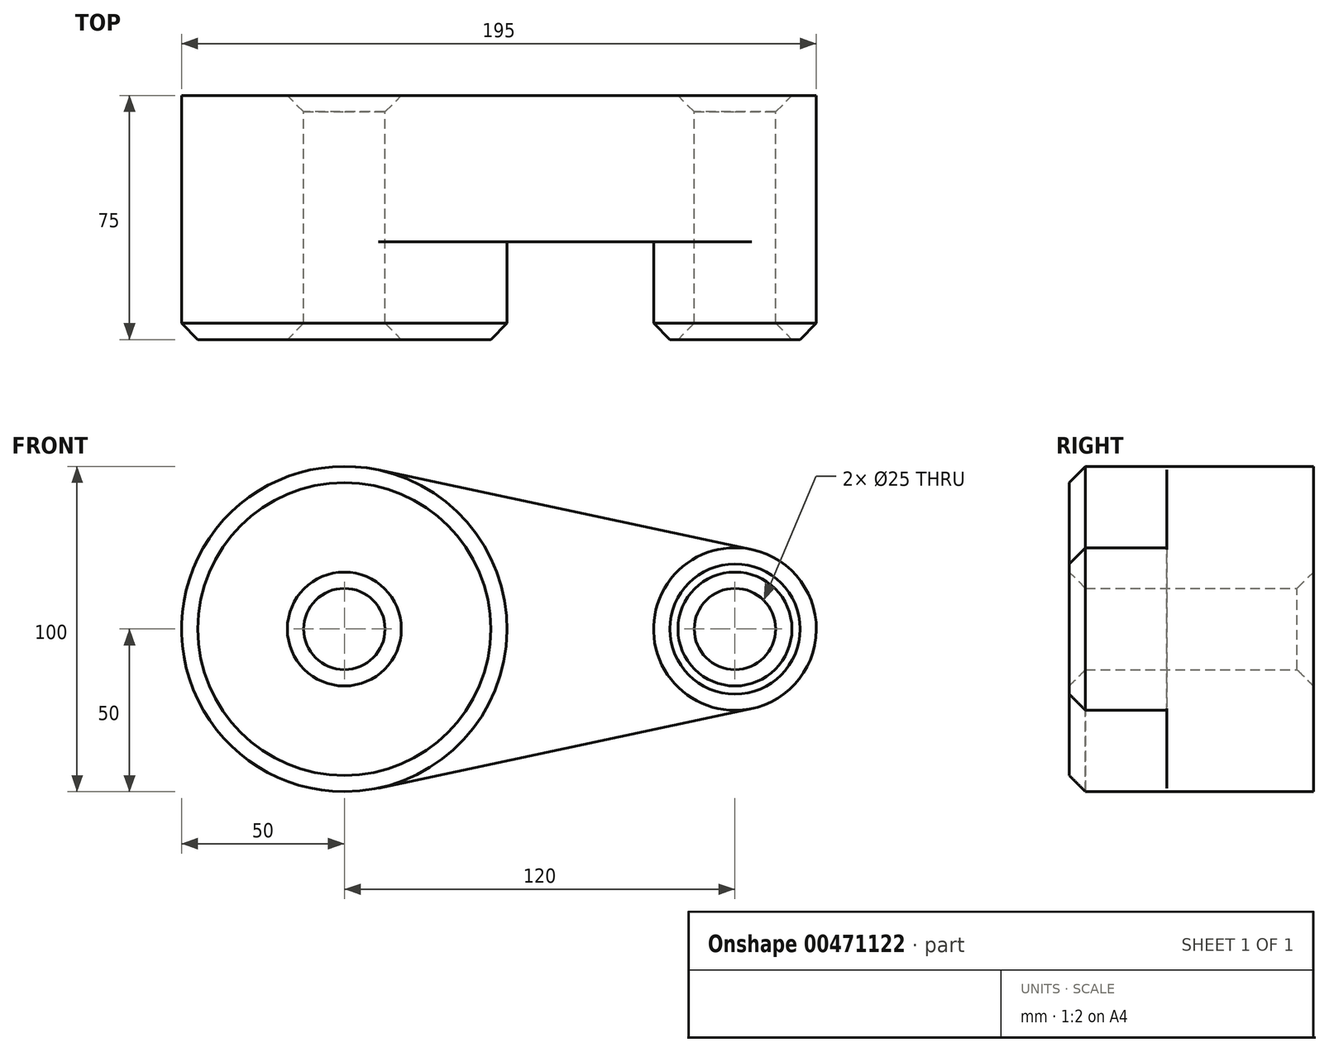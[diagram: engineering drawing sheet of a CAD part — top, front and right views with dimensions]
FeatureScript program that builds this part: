
annotation { "Feature Type Name" : "Feature", "Feature Type Description" : "" }
export const myFeature = defineFeature(function(context is Context, id is Id, definition is map)
    precondition{}
    {
        {
            var Q0;
            Q0=qCreatedBy(makeId("Front.planeOp"),FACE);
            var sketch = newSketch(context, id + "F0", { "sketchPlane" : qUnion([Q0])});
            skCircle(sketch, "E0", {"center": v(0, 0) * mm, "radius": 50 * mm});
            skCircle(sketch, "E1", {"center": v(120, 0) * mm, "radius": 25 * mm});
            skLineSegment(sketch, "E2", {"start": v(10.42, 48.9) * mm, "end": v(125.2, 24.45) * mm});
            skLineSegment(sketch, "E3", {"start": v(10.42, -48.9) * mm, "end": v(125.2, -24.45) * mm});
            skCircle(sketch, "E4", {"center": v(0, 0) * mm, "radius": 12.5 * mm});
            skCircle(sketch, "E5", {"center": v(120, 0) * mm, "radius": 12.5 * mm});
            skSolve(sketch);
        }
        {
            var Q0;
            Q0 = qSketchRegion(id + "F0", true);
            extrude(context, id + "F1", {"entities" : qUnion([Q0]), "depth" : 45 * mm});
        }
        {
            var Q0;
            Q0=makeQuery(id+"F0.imprint","IMPRINT",FACE,{"disambiguationData":[TD([[makeQuery(id+"F0.imprint","IMPRINT",EDGE,{"derivedFrom":sQuery(id+"F0.wireOp",EDGE,"E4")}),-1.0]])]});
            var Q1;
            Q1=makeQuery(id+"F0.imprint","IMPRINT",FACE,{"disambiguationData":[TD([[makeQuery(id+"F0.imprint","IMPRINT",EDGE,{"derivedFrom":sQuery(id+"F0.wireOp",EDGE,"E5")}),-1.0]])]});
            extrude(context, id + "F2", {"entities" : qUnion([Q0, Q1]), "operationType" : NewBodyOperationType.ADD, "depth" : 75 * mm});
        }
        {
            var Q0;
            Q0=makeQuery(id+"F2.opExtrude","CAP_EDGE",EDGE,{"disambiguationData":[OSD([sQuery(id+"F0.wireOp",EDGE,"E0")])],"isStart":false});
            var Q1;
            Q1=makeQuery(id+"F2.opExtrude","CAP_EDGE",EDGE,{"disambiguationData":[OSD([sQuery(id+"F0.wireOp",EDGE,"E4")])],"isStart":false});
            var Q2;
            Q2=makeQuery(id+"F2.opExtrude","CAP_EDGE",EDGE,{"disambiguationData":[OSD([sQuery(id+"F0.wireOp",EDGE,"E1")])],"isStart":false});
            var Q3;
            Q3=makeQuery(id+"F2.opExtrude","CAP_EDGE",EDGE,{"disambiguationData":[OSD([sQuery(id+"F0.wireOp",EDGE,"E5")])],"isStart":false});
            chamfer(context, id + "F3", {"entities" : qUnion([Q0, Q1, Q2, Q3]), "width" : 5 * mm, "tangentPropagation" : true});
        }
        {
            var Q0;
            Q0=makeQuery(id+"F1.opExtrude","CAP_EDGE",EDGE,{"disambiguationData":[OSD([sQuery(id+"F0.wireOp",EDGE,"E5")])],"isStart":true});
            var Q1;
            Q1=makeQuery(id+"F1.opExtrude","CAP_EDGE",EDGE,{"disambiguationData":[OSD([sQuery(id+"F0.wireOp",EDGE,"E4")])],"isStart":true});
            chamfer(context, id + "F4", {"entities" : qUnion([Q0, Q1]), "width" : 5 * mm, "tangentPropagation" : true});
        }
        {
            var Q0;
            {var subQ0=sQuery(id+"F0.wireOp",EDGE,"E2");Q0=makeQuery(id+"F0.imprint","IMPRINT",FACE,{"disambiguationData":[TD([[makeQuery(id+"F0.imprint","IMPRINT",EDGE,{"derivedFrom":subQ0}),-1.0]])]});}
            extrude(context, id + "F5", {"entities" : qUnion([Q0]), "operationType" : NewBodyOperationType.ADD, "depth" : 15 * mm});
        }
    });
